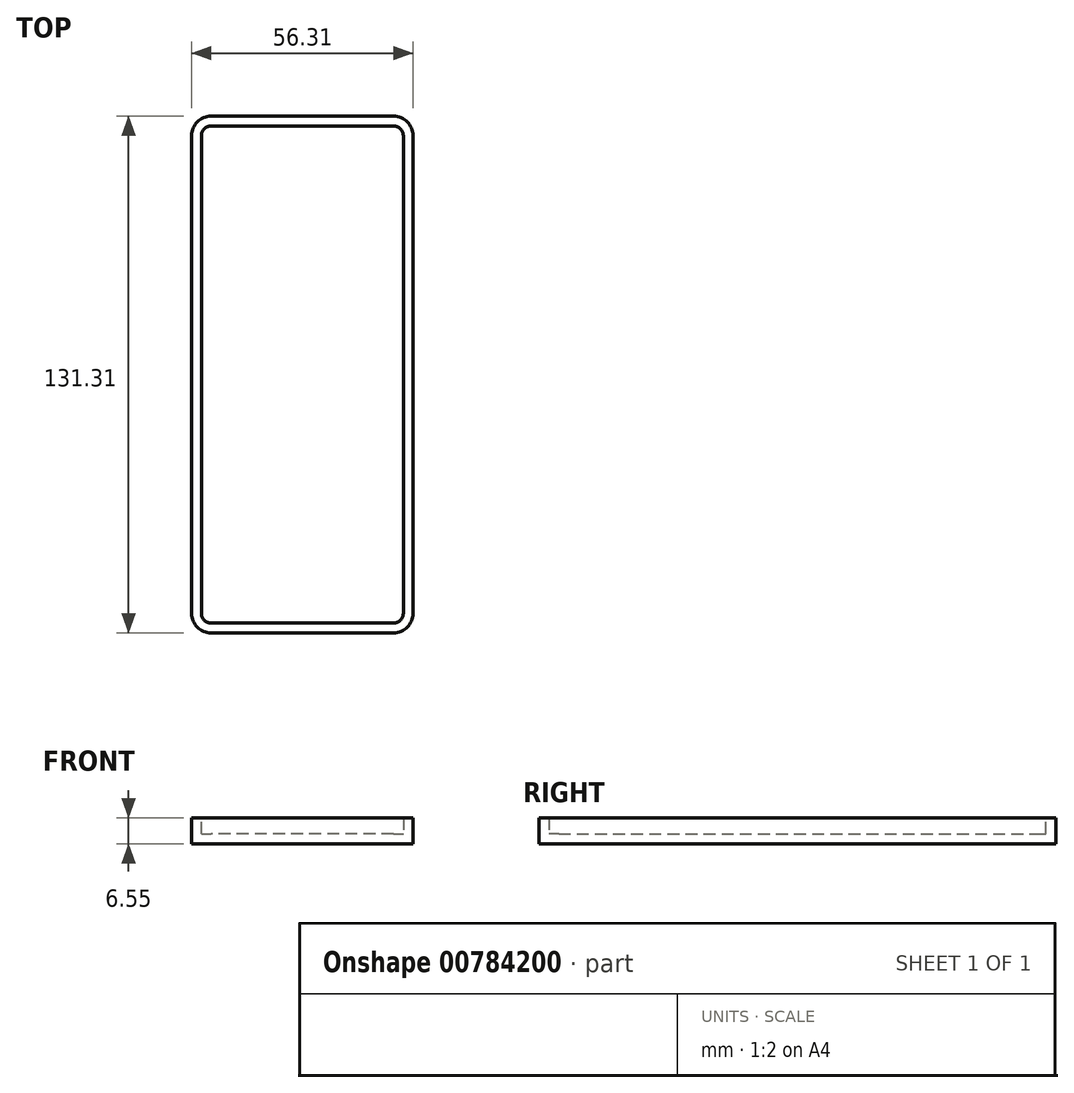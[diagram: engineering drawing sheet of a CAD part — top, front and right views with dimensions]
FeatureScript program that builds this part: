
annotation { "Feature Type Name" : "Feature", "Feature Type Description" : "" }
export const myFeature = defineFeature(function(context is Context, id is Id, definition is map)
    precondition{}
    {
        {
            var Q0;
            Q0=qCreatedBy(makeId("Top.planeOp"),FACE);
            var sketch = newSketch(context, id + "F0", { "sketchPlane" : qUnion([Q0])});
            skLineSegment(sketch, "E0", {"start": v(-34.53, -67.57) * mm, "end": v(-34.53, 63.74) * mm});
            skLineSegment(sketch, "E1", {"start": v(-34.53, 63.74) * mm, "end": v(21.78, 63.74) * mm});
            skLineSegment(sketch, "E2", {"start": v(21.78, 63.74) * mm, "end": v(21.78, -67.57) * mm});
            skLineSegment(sketch, "E3", {"start": v(21.78, -67.57) * mm, "end": v(-34.53, -67.57) * mm});
            skSolve(sketch);
        }
        {
            var Q0;
            Q0=makeQuery(id+"F0.imprint","IMPRINT",FACE,{"disambiguationData":[TD([[makeQuery(id+"F0.imprint","IMPRINT",EDGE,{"derivedFrom":sQuery(id+"F0.wireOp",EDGE,"E0")}),-1.0]])]});
            extrude(context, id + "F1", {"entities" : qUnion([Q0]), "depth" : 6.55 * mm, "offsetDistance" : 25 * mm});
        }
        {
            var Q0;
            Q0=makeQuery(id+"F1.opExtrude","SWEPT_EDGE",EDGE,{"disambiguationData":[OSD([sQuery(id+"F0.wireOp",EDGE,"E1"),sQuery(id+"F0.wireOp",EDGE,"E2")])]});
            var Q1;
            Q1=makeQuery(id+"F1.opExtrude","SWEPT_EDGE",EDGE,{"disambiguationData":[OSD([sQuery(id+"F0.wireOp",EDGE,"E2"),sQuery(id+"F0.wireOp",EDGE,"E3")])]});
            var Q2;
            Q2=makeQuery(id+"F1.opExtrude","SWEPT_EDGE",EDGE,{"disambiguationData":[OSD([sQuery(id+"F0.wireOp",EDGE,"E0"),sQuery(id+"F0.wireOp",EDGE,"E3")])]});
            var Q3;
            Q3=makeQuery(id+"F1.opExtrude","SWEPT_EDGE",EDGE,{"disambiguationData":[OSD([sQuery(id+"F0.wireOp",EDGE,"E0"),sQuery(id+"F0.wireOp",EDGE,"E1")])]});
            fillet(context, id + "F2", {"entities" : qUnion([Q0, Q1, Q2, Q3]), "radius" : 5 * mm, "tangentPropagation" : true, "allowEdgeOverflow" : false});
        }
        {
            var Q0;
            Q0=makeQuery(id+"F1.opExtrude","CAP_FACE",FACE,{"disambiguationData":[OSD([sQuery(id+"F0.wireOp",EDGE,"E0"),sQuery(id+"F0.wireOp",EDGE,"E1"),sQuery(id+"F0.wireOp",EDGE,"E2"),sQuery(id+"F0.wireOp",EDGE,"E3")])],"isStart":false});
            shell(context, id + "F3", {"entities" : qUnion([Q0]), "thickness" : 2.5 * mm});
        }
    });
